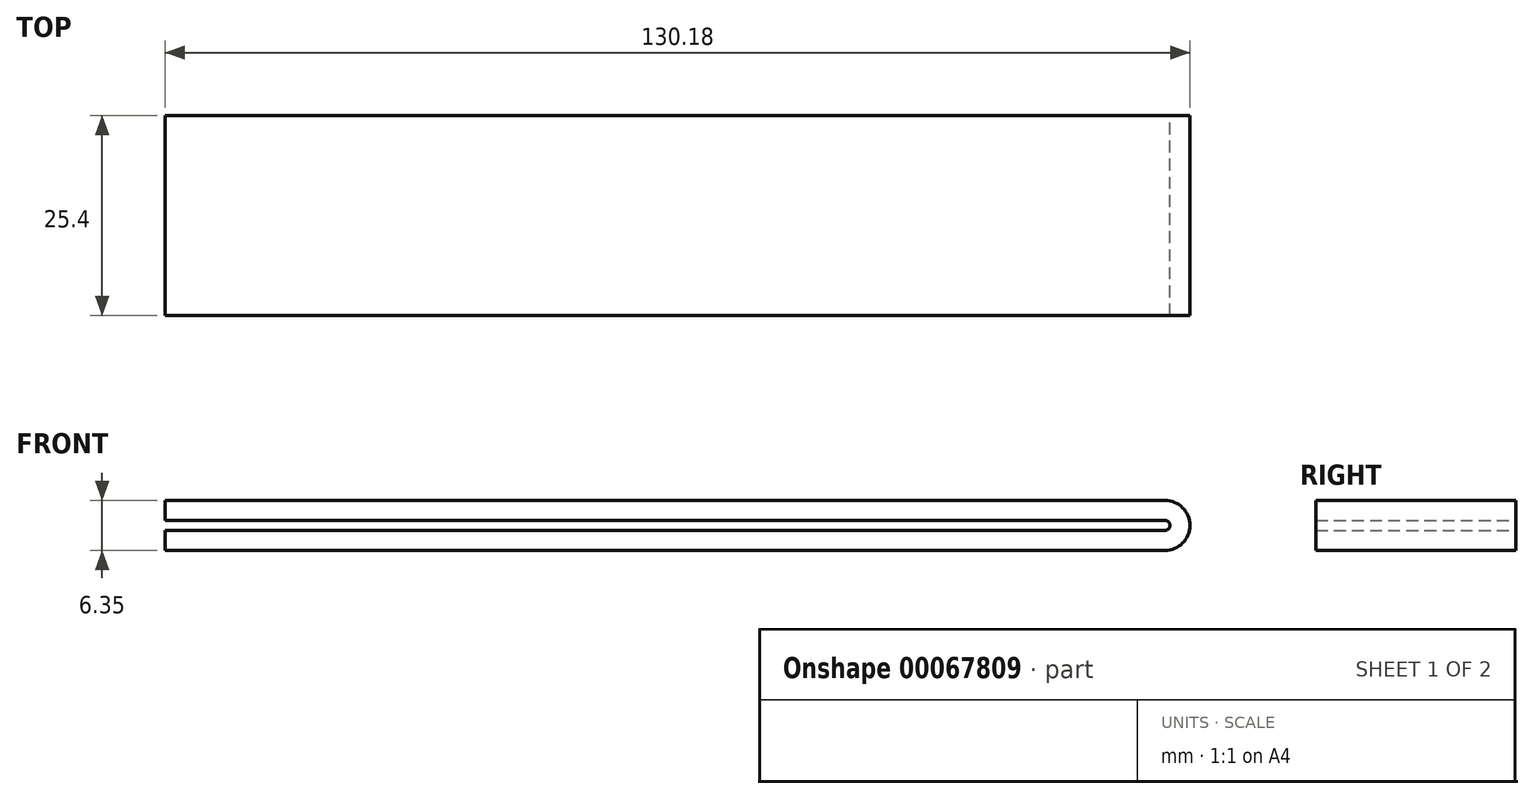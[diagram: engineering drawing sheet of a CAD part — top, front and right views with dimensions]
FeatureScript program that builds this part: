
annotation { "Feature Type Name" : "Feature", "Feature Type Description" : "" }
export const myFeature = defineFeature(function(context is Context, id is Id, definition is map)
    precondition{}
    {
        {
            var Q0;
            Q0=qCreatedBy(makeId("Front.planeOp"),FACE);
            var sketch = newSketch(context, id + "F0", { "sketchPlane" : qUnion([Q0])});
            skLineSegment(sketch, "E0", {"start": v(0, 0) * mm, "end": v(127, 0) * mm});
            skLineSegment(sketch, "E1", {"start": v(127, 2.54) * mm, "end": v(0, 2.54) * mm});
            skLineSegment(sketch, "E2", {"start": v(127, 3.8) * mm, "end": v(0, 3.8) * mm});
            skLineSegment(sketch, "E3", {"start": v(0, 6.35) * mm, "end": v(0, 3.8) * mm});
            skLineSegment(sketch, "E4", {"start": v(0, 6.35) * mm, "end": v(127, 6.35) * mm});
            skLineSegment(sketch, "E5", {"start": v(0, 2.54) * mm, "end": v(0, 0) * mm});
            skArc(sketch, "E6", {"start": v(127, 2.54) * mm, "mid": v(127.64, 3.17) * mm, "end": v(127, 3.8) * mm});
            skArc(sketch, "E7", {"start": v(127, 0) * mm, "mid": v(130.18, 3.18) * mm, "end": v(127, 6.35) * mm});
            skSolve(sketch);
        }
        {
            var Q0;
            Q0 = qSketchRegion(id + "F0", true);
            extrude(context, id + "F1", {"entities" : qUnion([Q0]), "depth" : 25.4 * mm});
        }
    });
